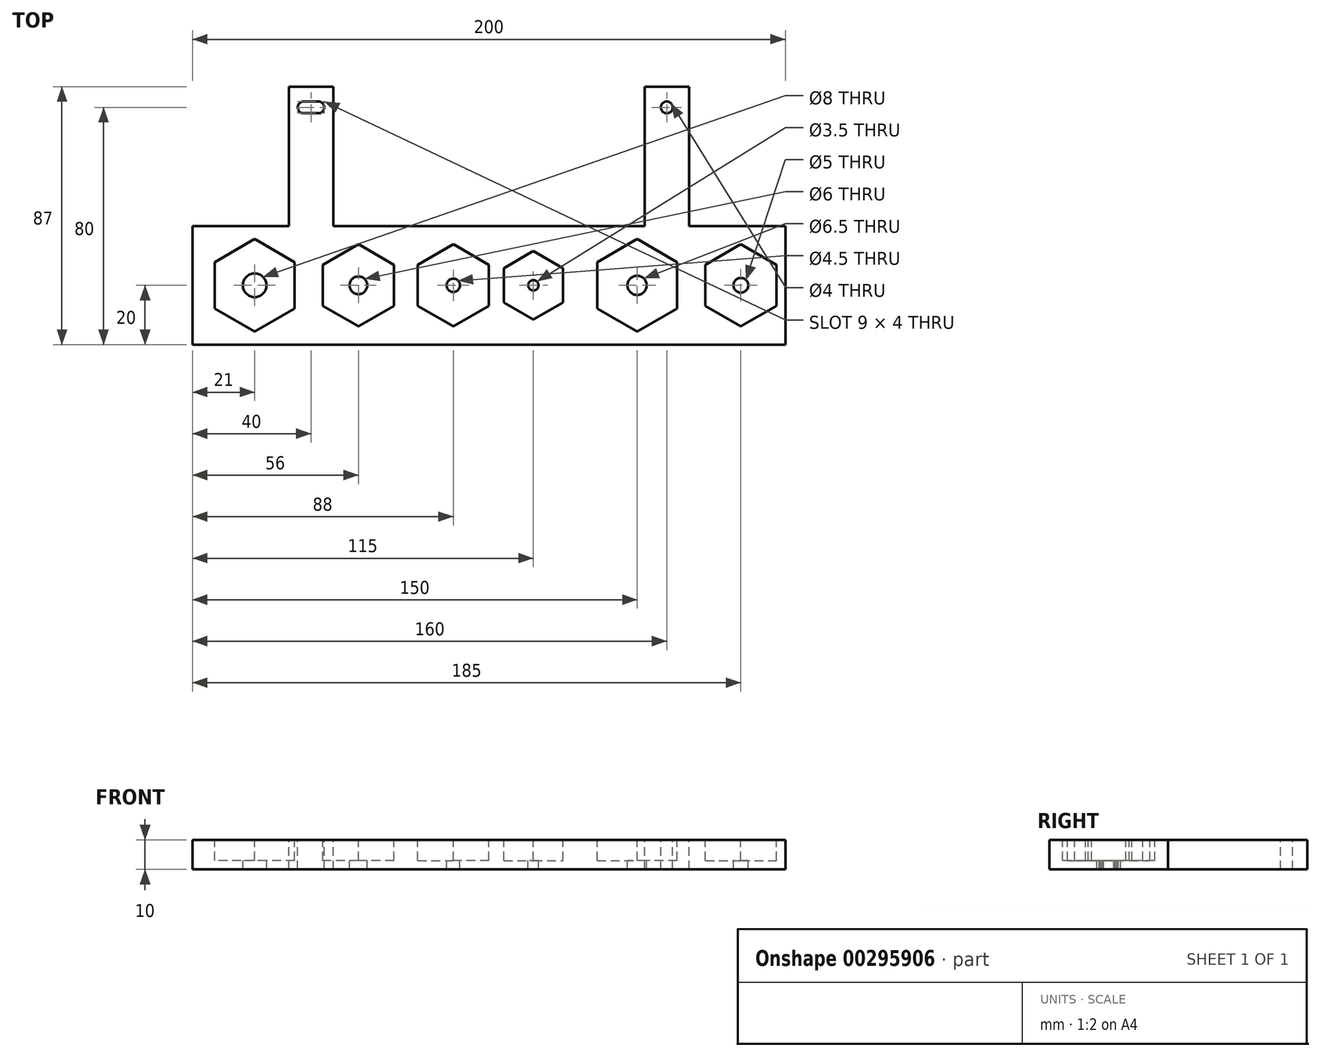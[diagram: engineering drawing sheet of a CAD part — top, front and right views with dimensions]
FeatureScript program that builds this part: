
annotation { "Feature Type Name" : "Feature", "Feature Type Description" : "" }
export const myFeature = defineFeature(function(context is Context, id is Id, definition is map)
    precondition{}
    {
        {
            var Q0;
            Q0=qCreatedBy(makeId("Top.planeOp"),FACE);
            var sketch = newSketch(context, id + "F0", { "sketchPlane" : qUnion([Q0])});
            skLineSegment(sketch, "E0.bottom", {"start": v(100, 20) * mm, "end": v(-100, 20) * mm});
            skLineSegment(sketch, "E0.top", {"start": v(100, -20) * mm, "end": v(-100, -20) * mm});
            skLineSegment(sketch, "E0.left", {"start": v(100, 20) * mm, "end": v(100, -20) * mm});
            skLineSegment(sketch, "E0.right", {"start": v(-100, 20) * mm, "end": v(-100, -20) * mm});
            skPoint(sketch, "E0.middle", {"position": v(0, 0) * mm});
            skSolve(sketch);
        }
        {
            var Q0;
            Q0 = qSketchRegion(id + "F0", true);
            extrude(context, id + "F1", {"entities" : qUnion([Q0]), "depth" : 10 * mm});
        }
        {
            var Q0;
            Q0=makeQuery(id+"F1.opExtrude","CAP_FACE",FACE,{"disambiguationData":[OSD([sQuery(id+"F0.wireOp",EDGE,"E0.bottom"),sQuery(id+"F0.wireOp",EDGE,"E0.top"),sQuery(id+"F0.wireOp",EDGE,"E0.left"),sQuery(id+"F0.wireOp",EDGE,"E0.right")])],"isStart":false});
            var sketch = newSketch(context, id + "F2", { "sketchPlane" : qUnion([Q0])});
            skCircle(sketch, "E1.cCircle", {"center": v(-79, 0) * mm, "radius": 13.5 * mm, "construction": true});
            skLineSegment(sketch, "E1.0", {"start": v(-79, -15.59) * mm, "end": v(-92.5, -7.8) * mm});
            skLineSegment(sketch, "E1.1", {"start": v(-92.5, -7.8) * mm, "end": v(-92.5, 7.8) * mm});
            skLineSegment(sketch, "E1.2", {"start": v(-92.5, 7.8) * mm, "end": v(-79, 15.59) * mm});
            skLineSegment(sketch, "E1.3", {"start": v(-79, 15.59) * mm, "end": v(-65.5, 7.8) * mm});
            skLineSegment(sketch, "E1.4", {"start": v(-65.5, 7.8) * mm, "end": v(-65.5, -7.8) * mm});
            skLineSegment(sketch, "E1.5", {"start": v(-65.5, -7.8) * mm, "end": v(-79, -15.59) * mm});
            skCircle(sketch, "E2.cCircle", {"center": v(85, 0) * mm, "radius": 12 * mm, "construction": true});
            skLineSegment(sketch, "E2.0", {"start": v(97, 6.93) * mm, "end": v(97, -6.93) * mm});
            skLineSegment(sketch, "E2.1", {"start": v(97, -6.93) * mm, "end": v(85, -13.86) * mm});
            skLineSegment(sketch, "E2.2", {"start": v(85, -13.86) * mm, "end": v(73, -6.93) * mm});
            skLineSegment(sketch, "E2.3", {"start": v(73, -6.93) * mm, "end": v(73, 6.93) * mm});
            skLineSegment(sketch, "E2.4", {"start": v(73, 6.93) * mm, "end": v(85, 13.86) * mm});
            skLineSegment(sketch, "E2.5", {"start": v(85, 13.86) * mm, "end": v(97, 6.93) * mm});
            skCircle(sketch, "E3.cCircle", {"center": v(-44, 0) * mm, "radius": 12 * mm, "construction": true});
            skLineSegment(sketch, "E3.0", {"start": v(-56, -6.93) * mm, "end": v(-56, 6.93) * mm});
            skLineSegment(sketch, "E3.1", {"start": v(-56, 6.93) * mm, "end": v(-44, 13.86) * mm});
            skLineSegment(sketch, "E3.2", {"start": v(-44, 13.86) * mm, "end": v(-32, 6.93) * mm});
            skLineSegment(sketch, "E3.3", {"start": v(-32, 6.93) * mm, "end": v(-32, -6.93) * mm});
            skLineSegment(sketch, "E3.4", {"start": v(-32, -6.93) * mm, "end": v(-44, -13.86) * mm});
            skLineSegment(sketch, "E3.5", {"start": v(-44, -13.86) * mm, "end": v(-56, -6.93) * mm});
            skCircle(sketch, "E4.cCircle", {"center": v(50, 0) * mm, "radius": 13.5 * mm, "construction": true});
            skLineSegment(sketch, "E4.0", {"start": v(63.5, -7.8) * mm, "end": v(50, -15.59) * mm});
            skLineSegment(sketch, "E4.1", {"start": v(50, -15.59) * mm, "end": v(36.5, -7.8) * mm});
            skLineSegment(sketch, "E4.2", {"start": v(36.5, -7.8) * mm, "end": v(36.5, 7.8) * mm});
            skLineSegment(sketch, "E4.3", {"start": v(36.5, 7.8) * mm, "end": v(50, 15.59) * mm});
            skLineSegment(sketch, "E4.4", {"start": v(50, 15.59) * mm, "end": v(63.5, 7.8) * mm});
            skLineSegment(sketch, "E4.5", {"start": v(63.5, 7.8) * mm, "end": v(63.5, -7.8) * mm});
            skCircle(sketch, "E5.cCircle", {"center": v(-12, 0) * mm, "radius": 12 * mm, "construction": true});
            skLineSegment(sketch, "E5.0", {"start": v(-24, 6.93) * mm, "end": v(-12, 13.86) * mm});
            skLineSegment(sketch, "E5.1", {"start": v(-12, 13.86) * mm, "end": v(0, 6.93) * mm});
            skLineSegment(sketch, "E5.2", {"start": v(0, 6.93) * mm, "end": v(0, -6.93) * mm});
            skLineSegment(sketch, "E5.3", {"start": v(0, -6.93) * mm, "end": v(-12, -13.86) * mm});
            skLineSegment(sketch, "E5.4", {"start": v(-12, -13.86) * mm, "end": v(-24, -6.93) * mm});
            skLineSegment(sketch, "E5.5", {"start": v(-24, -6.93) * mm, "end": v(-24, 6.93) * mm});
            skCircle(sketch, "E6.cCircle", {"center": v(15, 0) * mm, "radius": 10 * mm, "construction": true});
            skLineSegment(sketch, "E6.0", {"start": v(25, 5.77) * mm, "end": v(25, -5.77) * mm});
            skLineSegment(sketch, "E6.1", {"start": v(25, -5.77) * mm, "end": v(15, -11.55) * mm});
            skLineSegment(sketch, "E6.2", {"start": v(15, -11.55) * mm, "end": v(5, -5.77) * mm});
            skLineSegment(sketch, "E6.3", {"start": v(5, -5.77) * mm, "end": v(5, 5.77) * mm});
            skLineSegment(sketch, "E6.4", {"start": v(5, 5.77) * mm, "end": v(15, 11.55) * mm});
            skLineSegment(sketch, "E6.5", {"start": v(15, 11.55) * mm, "end": v(25, 5.77) * mm});
            skPoint(sketch, "E6.0.midPoint", {"position": v(25, 0) * mm});
            skSolve(sketch);
        }
        {
            var Q0;
            Q0 = qSketchRegion(id + "F2", true);
            extrude(context, id + "F3", {"entities" : qUnion([Q0]), "operationType" : NewBodyOperationType.REMOVE, "oppositeDirection" : true, "depth" : 7 * mm});
        }
        {
            var Q0;
            Q0=makeQuery(id+"F1.opExtrude","CAP_FACE",FACE,{"disambiguationData":[OSD([sQuery(id+"F0.wireOp",EDGE,"E0.bottom"),sQuery(id+"F0.wireOp",EDGE,"E0.top"),sQuery(id+"F0.wireOp",EDGE,"E0.left"),sQuery(id+"F0.wireOp",EDGE,"E0.right")])],"isStart":false});
            var sketch = newSketch(context, id + "F4", { "sketchPlane" : qUnion([Q0])});
            skCircle(sketch, "E7", {"center": v(-79, 0) * mm, "radius": 4 * mm});
            skCircle(sketch, "E8", {"center": v(-44, 0) * mm, "radius": 3 * mm});
            skCircle(sketch, "E9", {"center": v(-12, 0) * mm, "radius": 2.25 * mm});
            skCircle(sketch, "E10", {"center": v(15, 0) * mm, "radius": 1.75 * mm});
            skPoint(sketch, "E10.centerSnap0", {"position": v(5, 0) * mm});
            skCircle(sketch, "E11", {"center": v(50, 0) * mm, "radius": 3.25 * mm});
            skCircle(sketch, "E12", {"center": v(85, 0) * mm, "radius": 2.5 * mm});
            skSolve(sketch);
        }
        {
            var Q0;
            Q0 = qSketchRegion(id + "F4", true);
            extrude(context, id + "F5", {"entities" : qUnion([Q0]), "operationType" : NewBodyOperationType.REMOVE, "endBound" : BoundingType.THROUGH_ALL, "oppositeDirection" : true, "depth" : 25 * mm});
        }
        {
            var Q0;
            Q0=makeQuery(id+"F1.opExtrude","CAP_FACE",FACE,{"disambiguationData":[OSD([sQuery(id+"F0.wireOp",EDGE,"E0.bottom"),sQuery(id+"F0.wireOp",EDGE,"E0.top"),sQuery(id+"F0.wireOp",EDGE,"E0.left"),sQuery(id+"F0.wireOp",EDGE,"E0.right")])],"isStart":false});
            var sketch = newSketch(context, id + "F6", { "sketchPlane" : qUnion([Q0])});
            skLineSegment(sketch, "E13.bottom", {"start": v(67.5, 20) * mm, "end": v(52.5, 20) * mm});
            skLineSegment(sketch, "E13.top", {"start": v(67.5, 67) * mm, "end": v(52.5, 67) * mm});
            skLineSegment(sketch, "E13.left", {"start": v(67.5, 20) * mm, "end": v(67.5, 67) * mm});
            skLineSegment(sketch, "E13.right", {"start": v(52.5, 20) * mm, "end": v(52.5, 67) * mm});
            skLineSegment(sketch, "E14", {"start": v(0, 0) * mm, "end": v(0, 39.94) * mm, "construction": true});
            skPoint(sketch, "E14.endSnap0", {"position": v(0, 20) * mm});
            skLineSegment(sketch, "E15.MirrorCS", {"start": v(-67.5, 20) * mm, "end": v(-52.5, 20) * mm});
            skLineSegment(sketch, "E16.MirrorCS", {"start": v(-67.5, 67) * mm, "end": v(-52.5, 67) * mm});
            skLineSegment(sketch, "E17.MirrorCS", {"start": v(-67.5, 20) * mm, "end": v(-67.5, 67) * mm});
            skLineSegment(sketch, "E18.MirrorCS", {"start": v(-52.5, 20) * mm, "end": v(-52.5, 67) * mm});
            skCircle(sketch, "E19", {"center": v(60, 60) * mm, "radius": 2 * mm});
            skPoint(sketch, "E19.centerSnap0", {"position": v(60, 67) * mm});
            skLineSegment(sketch, "E20", {"start": v(-60, 67) * mm, "end": v(-60, 20) * mm, "construction": true});
            skLineSegment(sketch, "E21", {"start": v(60, 60) * mm, "end": v(-60, 60) * mm, "construction": true});
            skArc(sketch, "E22", {"start": v(-57.5, 58) * mm, "mid": v(-55.5, 60) * mm, "end": v(-57.5, 62) * mm});
            skArc(sketch, "E23.MirrorC", {"start": v(-62.5, 58) * mm, "mid": v(-64.5, 60) * mm, "end": v(-62.5, 62) * mm});
            skLineSegment(sketch, "E24", {"start": v(-57.5, 58) * mm, "end": v(-62.5, 58) * mm});
            skLineSegment(sketch, "E25", {"start": v(-62.5, 62) * mm, "end": v(-57.5, 62) * mm});
            skSolve(sketch);
        }
        {
            var Q0;
            Q0 = qSketchRegion(id + "F6", true);
            var Q1;
            Q1=makeQuery(id+"F1.opExtrude","CAP_FACE",FACE,{"disambiguationData":[OSD([sQuery(id+"F0.wireOp",EDGE,"E0.bottom"),sQuery(id+"F0.wireOp",EDGE,"E0.top"),sQuery(id+"F0.wireOp",EDGE,"E0.left"),sQuery(id+"F0.wireOp",EDGE,"E0.right")])],"isStart":true});
            extrude(context, id + "F7", {"entities" : qUnion([Q0]), "operationType" : NewBodyOperationType.ADD, "endBound" : BoundingType.UP_TO_SURFACE, "oppositeDirection" : true, "endBoundEntityFace" : qUnion([Q1]), "depth" : 25 * mm});
        }
    });
